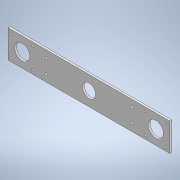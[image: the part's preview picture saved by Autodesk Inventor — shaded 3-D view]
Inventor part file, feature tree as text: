
AUTODESK INVENTOR PART (.ipt)
format: ipt  version: 2021 (Build 250183000, 183)  size: 139,264 bytes
history: native  units: mm
features: other x9, sketch x4, hole x4, extrude x1, mirror x1
ambient origin geometry x8: Origin, YZ Plane, XZ Plane, XY Plane, X Axis, Y Axis, Z Axis, Center Point
bodies: Body1 (feature_tree)
feature tree (19):
  other  "Sólido1"
  extrude  "Extrusão1"  Depth=42.0mm
  sketch  "Esboço2"  dims[d2=3.0mm d3=0.0mm d4=42.0mm]
  hole  "Furo1"  [1 undecoded]
  hole  "Furo2"  [1 undecoded]
  mirror  "Espelhamento1"
  hole  "Furo3"  [1 undecoded]
  hole  "Furo4"  [1 undecoded]
  sketch  "Esboço1"  dims[d0=242.0mm d1=42.0mm]
  sketch  "Esboço3"  dims[d5=42.0mm d6=31.0mm]
  other  "Referência1"
  other  "Referência2"
  other  "Referência3"
  other  "Referência4"
  sketch  "Esboço4"  dims[d7=31.0mm d8=3.0mm d9=6.0mm d10=4.0mm d11=2.0mm d12=90.0deg d13=8.0mm d14=20.594885mm d15=23.0mm d16=6.0mm d17=4.0mm d18=2.0mm d19=90.0deg d20=8.0mm d21=20.594885mm d22=4.0mm d23=8.0mm d24=4.0mm d25=2.0mm d26=90.0deg d27=8.0mm d28=20.594885mm d29=21.0mm d30=121.0mm d31=20.0mm d32=6.0mm d33=4.0mm d34=2.0mm d35=90.0deg d36=8.0mm d37=20.594885mm]
  parser-record x1  (decoder bookkeeping rows leaked as tree rows — omitted from the tree; the rows remain in map.json)
  other  "Omni Robot.iam"
  other  "chapa central:2"
  other  "chapa central:1"
note: 4 required parameter values undecoded (feature->parameter linkage not recoverable at this tier; creation-order binding heuristic only, values carry confidence <= 0.55)
note: 1 file-system path scrubbed to <path> (originals preserved in map.json)
